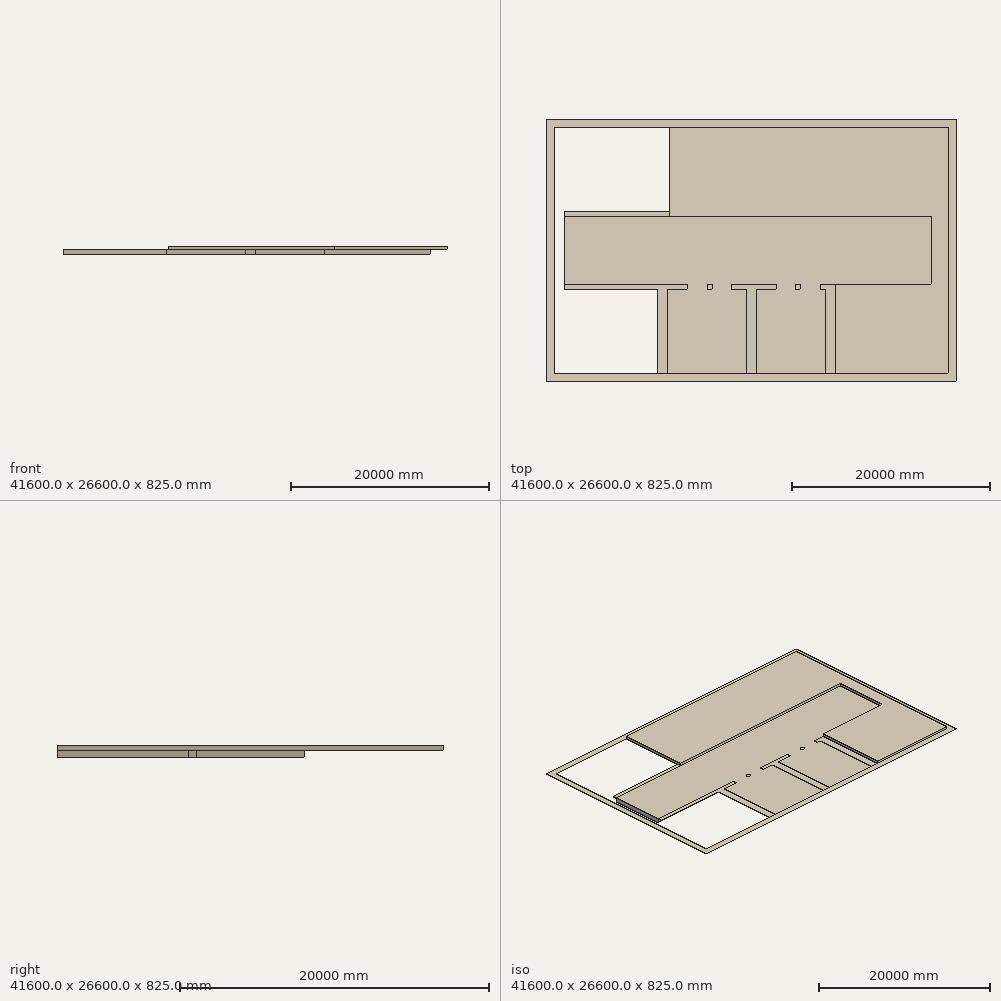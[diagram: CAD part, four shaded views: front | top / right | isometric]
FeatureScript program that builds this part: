
annotation { "Feature Type Name" : "Feature", "Feature Type Description" : "" }
export const myFeature = defineFeature(function(context is Context, id is Id, definition is map)
    precondition{}
    {
        {
            assignVariable(context, id + "F0", {"name" : "m", "anyValue" : 1});
        }
        {
            var Q0;
            Q0=qCreatedBy(makeId("Top.planeOp"),FACE);
            var sketch = newSketch(context, id + "F1", { "sketchPlane" : qUnion([Q0])});
            skLineSegment(sketch, "E0.bottom", {"start": v(-20000, -12500) * mm, "end": v(20000, -12500) * mm, "construction": true});
            skLineSegment(sketch, "E0.top", {"start": v(-20000, 12500) * mm, "end": v(20000, 12500) * mm, "construction": true});
            skLineSegment(sketch, "E0.left", {"start": v(-20000, -12500) * mm, "end": v(-20000, 12500) * mm, "construction": true});
            skLineSegment(sketch, "E0.right", {"start": v(20000, -12500) * mm, "end": v(20000, 12500) * mm, "construction": true});
            skPoint(sketch, "E0.middle", {"position": v(0, 0) * mm});
            skLineSegment(sketch, "E1", {"start": v(-19000, 3500) * mm, "end": v(6200, 3500) * mm});
            skLineSegment(sketch, "E2", {"start": v(-19000, -3500) * mm, "end": v(-9000, -3500) * mm});
            skPoint(sketch, "E2.endSnap0", {"position": v(20000, 0) * mm});
            skLineSegment(sketch, "E3", {"start": v(18800, 3500) * mm, "end": v(18800, -3500) * mm});
            skLineSegment(sketch, "E4", {"start": v(8000, 3500) * mm, "end": v(8000, 12500) * mm});
            skLineSegment(sketch, "E5", {"start": v(6200, 3500) * mm, "end": v(6200, 8500) * mm});
            skLineSegment(sketch, "E6", {"start": v(0, 4000) * mm, "end": v(0, 12500) * mm});
            skLineSegment(sketch, "E7", {"start": v(8000, -3500) * mm, "end": v(8000, -12500) * mm});
            skLineSegment(sketch, "E8", {"start": v(-9000, -3500) * mm, "end": v(-9000, -12500) * mm});
            skLineSegment(sketch, "E9.trimOffspring", {"start": v(8000, 3500) * mm, "end": v(18800, 3500) * mm});
            skLineSegment(sketch, "E10", {"start": v(3000, 8500) * mm, "end": v(3000, 12500) * mm});
            skPoint(sketch, "E11.start.orphan", {"position": v(6200, 12500) * mm});
            skLineSegment(sketch, "E12", {"start": v(0, -3500) * mm, "end": v(0, -12500) * mm});
            skLineSegment(sketch, "E13", {"start": v(3000, 8500) * mm, "end": v(8000, 8500) * mm});
            skLineSegment(sketch, "E14", {"start": v(-19000, 4000) * mm, "end": v(-500, 4000) * mm});
            skLineSegment(sketch, "E15", {"start": v(-500, 4000) * mm, "end": v(-500, 12500) * mm});
            skLineSegment(sketch, "E16", {"start": v(2500, 12500) * mm, "end": v(2500, 8000) * mm});
            skLineSegment(sketch, "E17", {"start": v(2500, 8000) * mm, "end": v(5700, 8000) * mm});
            skLineSegment(sketch, "E18", {"start": v(0, 4000) * mm, "end": v(5700, 4000) * mm});
            skLineSegment(sketch, "E19", {"start": v(8500, 12500) * mm, "end": v(8500, 4000) * mm});
            skLineSegment(sketch, "E20", {"start": v(8500, 4000) * mm, "end": v(18800, 4000) * mm});
            skLineSegment(sketch, "E21", {"start": v(5700, 8000) * mm, "end": v(5700, 4000) * mm});
            skPoint(sketch, "E21.endSnap0", {"position": v(3100, 4000) * mm});
            skLineSegment(sketch, "E22", {"start": v(18300, 3500) * mm, "end": v(18300, -3500) * mm});
            skLineSegment(sketch, "E23", {"start": v(8500, -12500) * mm, "end": v(8500, -4000) * mm});
            skLineSegment(sketch, "E24", {"start": v(8500, -4000) * mm, "end": v(9000, -4000) * mm});
            skLineSegment(sketch, "E25", {"start": v(-8500, -12500) * mm, "end": v(-8500, -4000) * mm});
            skLineSegment(sketch, "E26", {"start": v(-8500, -4000) * mm, "end": v(-6500, -4000) * mm});
            skLineSegment(sketch, "E27", {"start": v(-500, -4000) * mm, "end": v(-500, -12500) * mm});
            skLineSegment(sketch, "E28", {"start": v(-19000, -4000) * mm, "end": v(-9500, -4000) * mm});
            skLineSegment(sketch, "E29", {"start": v(-9500, -4000) * mm, "end": v(-9500, -12500) * mm});
            skLineSegment(sketch, "E30", {"start": v(500, -12500) * mm, "end": v(500, -4000) * mm});
            skLineSegment(sketch, "E31", {"start": v(500, -4000) * mm, "end": v(2500, -4000) * mm});
            skLineSegment(sketch, "E32", {"start": v(7500, -4000) * mm, "end": v(7500, -12500) * mm});
            skLineSegment(sketch, "E33", {"start": v(18800, 3500) * mm, "end": v(18800, 4000) * mm});
            skPoint(sketch, "E34.orphan", {"position": v(20000, -3500) * mm});
            skLineSegment(sketch, "E35", {"start": v(18800, -3500) * mm, "end": v(18800, -4000) * mm});
            skPoint(sketch, "E36.orphan", {"position": v(6200, 4000) * mm});
            skLineSegment(sketch, "E37", {"start": v(-500, -12500) * mm, "end": v(500, -12500) * mm});
            skLineSegment(sketch, "E38", {"start": v(-9500, -12500) * mm, "end": v(-8500, -12500) * mm});
            skLineSegment(sketch, "E39", {"start": v(-20000, -12500) * mm, "end": v(-19500, -12500) * mm});
            skLineSegment(sketch, "E40", {"start": v(-500, 12500) * mm, "end": v(0, 12500) * mm});
            skLineSegment(sketch, "E41", {"start": v(-20000, 3500) * mm, "end": v(-20000, 4000) * mm});
            skLineSegment(sketch, "E42", {"start": v(2500, 12500) * mm, "end": v(3000, 12500) * mm});
            skLineSegment(sketch, "E43", {"start": v(8000, 12500) * mm, "end": v(8500, 12500) * mm});
            skLineSegment(sketch, "E44", {"start": v(7500, -12500) * mm, "end": v(8500, -12500) * mm});
            skLineSegment(sketch, "E45", {"start": v(-20000, -3500) * mm, "end": v(-20000, -12500) * mm});
            skLineSegment(sketch, "E46", {"start": v(-19000, 3500) * mm, "end": v(-19000, -3500) * mm});
            skLineSegment(sketch, "E47", {"start": v(-19000, -3500) * mm, "end": v(-19000, -4000) * mm});
            skLineSegment(sketch, "E48", {"start": v(-19000, 3500) * mm, "end": v(-19000, 4000) * mm});
            skLineSegment(sketch, "E49", {"start": v(9000, -4000) * mm, "end": v(9000, -3500) * mm});
            skLineSegment(sketch, "E50", {"start": v(11000, -4000) * mm, "end": v(11000, -3500) * mm});
            skLineSegment(sketch, "E51.trimOffspring", {"start": v(11000, -4000) * mm, "end": v(18800, -4000) * mm});
            skLineSegment(sketch, "E52.trimOffspring", {"start": v(11000, -3500) * mm, "end": v(18300, -3500) * mm});
            skLineSegment(sketch, "E53", {"start": v(9000, 4000) * mm, "end": v(9000, 3500) * mm});
            skLineSegment(sketch, "E54", {"start": v(11000, 4000) * mm, "end": v(11000, 3500) * mm});
            skLineSegment(sketch, "E55", {"start": v(5700, 8000) * mm, "end": v(6200, 8000) * mm});
            skLineSegment(sketch, "E56", {"start": v(5700, 7000) * mm, "end": v(6200, 7000) * mm});
            skLineSegment(sketch, "E57", {"start": v(-9000, 4000) * mm, "end": v(-9000, 12500) * mm});
            skLineSegment(sketch, "E58", {"start": v(-11000, 4000) * mm, "end": v(-11000, 3500) * mm});
            skLineSegment(sketch, "E59", {"start": v(-9000, 4000) * mm, "end": v(-9000, 3500) * mm});
            skLineSegment(sketch, "E60", {"start": v(-6500, -4000) * mm, "end": v(-6500, -3500) * mm});
            skPoint(sketch, "E60.endSnap0", {"position": v(-5000, -3500) * mm});
            skLineSegment(sketch, "E61", {"start": v(-4500, -3500) * mm, "end": v(-4500, -4000) * mm});
            skLineSegment(sketch, "E62", {"start": v(-4000, -3500) * mm, "end": v(-4000, -4000) * mm});
            skLineSegment(sketch, "E63", {"start": v(-2000, -3500) * mm, "end": v(-2000, -4000) * mm});
            skLineSegment(sketch, "E64.trimOffspring", {"start": v(-4500, -4000) * mm, "end": v(-4000, -4000) * mm});
            skLineSegment(sketch, "E65.trimOffspring", {"start": v(-5000, -3500) * mm, "end": v(-4000, -3500) * mm});
            skLineSegment(sketch, "E66.trimOffspring", {"start": v(-2000, -3500) * mm, "end": v(2500, -3500) * mm});
            skLineSegment(sketch, "E67.trimOffspring", {"start": v(-2000, -4000) * mm, "end": v(-500, -4000) * mm});
            skLineSegment(sketch, "E68", {"start": v(2500, -3500) * mm, "end": v(2500, -4000) * mm});
            skLineSegment(sketch, "E69", {"start": v(4500, -3500) * mm, "end": v(4500, -4000) * mm});
            skLineSegment(sketch, "E70", {"start": v(5000, -3500) * mm, "end": v(5000, -4000) * mm});
            skLineSegment(sketch, "E71", {"start": v(7000, -3500) * mm, "end": v(7000, -4000) * mm});
            skLineSegment(sketch, "E72.trimOffspring", {"start": v(4500, -4000) * mm, "end": v(5000, -4000) * mm});
            skLineSegment(sketch, "E73.trimOffspring", {"start": v(4500, -3500) * mm, "end": v(5000, -3500) * mm});
            skLineSegment(sketch, "E74.trimOffspring", {"start": v(7000, -3500) * mm, "end": v(9000, -3500) * mm});
            skLineSegment(sketch, "E75.trimOffspring", {"start": v(7000, -4000) * mm, "end": v(7500, -4000) * mm});
            skLineSegment(sketch, "E76", {"start": v(-6500, -3500) * mm, "end": v(-9000, -3500) * mm});
            skSolve(sketch);
        }
        {
            var Q0;
            Q0 = qSketchRegion(id + "F1", true);
            extrude(context, id + "F2", {"entities" : qUnion([Q0]), "depth" : (getVariable(context, 'm') * 5) * mm});
        }
        {
            var Q0;
            Q0=qCreatedBy(makeId("Top.planeOp"),FACE);
            var sketch = newSketch(context, id + "F3", { "sketchPlane" : qUnion([Q0])});
            skLineSegment(sketch, "E77.bottom", {"start": v(-20000, 12500) * mm, "end": v(20000, 12500) * mm});
            skLineSegment(sketch, "E77.top", {"start": v(-20000, -12500) * mm, "end": v(20000, -12500) * mm});
            skLineSegment(sketch, "E77.left", {"start": v(-20000, 12500) * mm, "end": v(-20000, -12500) * mm});
            skLineSegment(sketch, "E77.right", {"start": v(20000, 12500) * mm, "end": v(20000, -12500) * mm});
            skPoint(sketch, "E77.middle", {"position": v(0, 0) * mm});
            skLineSegment(sketch, "E78.bottom", {"start": v(-20800, 13300) * mm, "end": v(20800, 13300) * mm});
            skLineSegment(sketch, "E78.top", {"start": v(-20800, -13300) * mm, "end": v(20800, -13300) * mm});
            skLineSegment(sketch, "E78.left", {"start": v(-20800, 13300) * mm, "end": v(-20800, -13300) * mm});
            skLineSegment(sketch, "E78.right", {"start": v(20800, 13300) * mm, "end": v(20800, -13300) * mm});
            skSolve(sketch);
        }
        {
            var Q0;
            Q0 = qSketchRegion(id + "F3", true);
            extrude(context, id + "F4", {"entities" : qUnion([Q0]), "depth" : (getVariable(context, 'm') * 5) * mm, "offsetDistance" : 25 * mm});
        }
        {
            var Q0;
            Q0=makeQuery(id+"F4.boolean.opBoolean","MERGE",FACE,{"derivedFrom":[makeQuery(id+"F2.opExtrude","CAP_FACE",FACE,{"disambiguationData":[OSD([sQuery(id+"F1.wireOp",EDGE,"E1"),sQuery(id+"F1.wireOp",EDGE,"E5"),sQuery(id+"F1.wireOp",EDGE,"E6"),sQuery(id+"F1.wireOp",EDGE,"E10"),sQuery(id+"F1.wireOp",EDGE,"E13"),sQuery(id+"F1.wireOp",EDGE,"E14"),sQuery(id+"F1.wireOp",EDGE,"E15"),sQuery(id+"F1.wireOp",EDGE,"E16"),sQuery(id+"F1.wireOp",EDGE,"E17"),sQuery(id+"F1.wireOp",EDGE,"E18"),sQuery(id+"F1.wireOp",EDGE,"E21"),sQuery(id+"F1.wireOp",EDGE,"E40"),sQuery(id+"F1.wireOp",EDGE,"E41"),sQuery(id+"F1.wireOp",EDGE,"E42")])],"isStart":true}),makeQuery(id+"F2.opExtrude","CAP_FACE",FACE,{"disambiguationData":[OSD([sQuery(id+"F1.wireOp",EDGE,"E2"),sQuery(id+"F1.wireOp",EDGE,"E3"),sQuery(id+"F1.wireOp",EDGE,"E4"),sQuery(id+"F1.wireOp",EDGE,"E9.trimOffspring"),sQuery(id+"F1.wireOp",EDGE,"E19"),sQuery(id+"F1.wireOp",EDGE,"E20"),sQuery(id+"F1.wireOp",EDGE,"E22"),sQuery(id+"F1.wireOp",EDGE,"E23"),sQuery(id+"F1.wireOp",EDGE,"E24"),sQuery(id+"F1.wireOp",EDGE,"E25"),sQuery(id+"F1.wireOp",EDGE,"E26"),sQuery(id+"F1.wireOp",EDGE,"E27"),sQuery(id+"F1.wireOp",EDGE,"Nue6VRTW-FETu-XBWY-EpAh-Sq0DysgrU8W1"),sQuery(id+"F1.wireOp",EDGE,"E28"),sQuery(id+"F1.wireOp",EDGE,"E29"),sQuery(id+"F1.wireOp",EDGE,"E30"),sQuery(id+"F1.wireOp",EDGE,"E31"),sQuery(id+"F1.wireOp",EDGE,"E32"),sQuery(id+"F1.wireOp",EDGE,"E33"),sQuery(id+"F1.wireOp",EDGE,"E35"),sQuery(id+"F1.wireOp",EDGE,"E37"),sQuery(id+"F1.wireOp",EDGE,"E38"),sQuery(id+"F1.wireOp",EDGE,"E43"),sQuery(id+"F1.wireOp",EDGE,"E44"),sQuery(id+"F1.wireOp",EDGE,"E39"),sQuery(id+"F1.wireOp",EDGE,"E45")])],"isStart":true}),makeQuery(id+"F4.opExtrude","CAP_FACE",FACE,{"disambiguationData":[OSD([sQuery(id+"F3.wireOp",EDGE,"E77.bottom"),sQuery(id+"F3.wireOp",EDGE,"E77.top"),sQuery(id+"F3.wireOp",EDGE,"E77.left"),sQuery(id+"F3.wireOp",EDGE,"E77.right"),sQuery(id+"F3.wireOp",EDGE,"E78.bottom"),sQuery(id+"F3.wireOp",EDGE,"E78.top"),sQuery(id+"F3.wireOp",EDGE,"E78.left"),sQuery(id+"F3.wireOp",EDGE,"E78.right")])],"isStart":true})]});
            var sketch = newSketch(context, id + "F5", { "sketchPlane" : qUnion([Q0])});
            skLineSegment(sketch, "E79.bottom", {"start": v(-19000, -3500) * mm, "end": v(18300, -3500) * mm});
            skLineSegment(sketch, "E79.top", {"start": v(-19000, 3500) * mm, "end": v(-6500, 3500) * mm});
            skLineSegment(sketch, "E79.left", {"start": v(-19000, -3500) * mm, "end": v(-19000, 3500) * mm});
            skLineSegment(sketch, "E79.right", {"start": v(18300, -3500) * mm, "end": v(18300, 3500) * mm});
            skLineSegment(sketch, "E80.bottom", {"start": v(-8500, 4000) * mm, "end": v(-6500, 4000) * mm});
            skLineSegment(sketch, "E80.top", {"start": v(-8500, 12500) * mm, "end": v(-500, 12500) * mm});
            skLineSegment(sketch, "E80.left", {"start": v(-8500, 4000) * mm, "end": v(-8500, 12500) * mm});
            skLineSegment(sketch, "E80.right", {"start": v(-500, 4000) * mm, "end": v(-500, 12500) * mm});
            skLineSegment(sketch, "E81.bottom", {"start": v(500, 4000) * mm, "end": v(2500, 4000) * mm});
            skLineSegment(sketch, "E81.top", {"start": v(500, 12500) * mm, "end": v(7500, 12500) * mm});
            skLineSegment(sketch, "E81.left", {"start": v(500, 4000) * mm, "end": v(500, 12500) * mm});
            skLineSegment(sketch, "E81.right", {"start": v(7500, 4000) * mm, "end": v(7500, 12500) * mm});
            skLineSegment(sketch, "E82", {"start": v(-6500, 4000) * mm, "end": v(-6500, 3500) * mm});
            skLineSegment(sketch, "E83", {"start": v(-4500, 3500) * mm, "end": v(-4500, 4000) * mm});
            skLineSegment(sketch, "E84", {"start": v(-4000, 3500) * mm, "end": v(-4000, 4000) * mm});
            skLineSegment(sketch, "E85", {"start": v(-500, 4000) * mm, "end": v(500, 4000) * mm, "construction": true});
            skLineSegment(sketch, "E86", {"start": v(0, 4000) * mm, "end": v(0, 3500) * mm, "construction": true});
            skLineSegment(sketch, "E87", {"start": v(-2000, 3500) * mm, "end": v(-2000, 4000) * mm});
            skLineSegment(sketch, "E88.MirrorCS", {"start": v(4500, 3500) * mm, "end": v(4500, 4000) * mm});
            skLineSegment(sketch, "E89", {"start": v(2500, 3500) * mm, "end": v(2500, 4000) * mm});
            skLineSegment(sketch, "E90", {"start": v(5000, 3500) * mm, "end": v(5000, 4000) * mm});
            skLineSegment(sketch, "E91", {"start": v(7000, 3500) * mm, "end": v(7000, 4000) * mm});
            skLineSegment(sketch, "E92.trimOffspring", {"start": v(-4500, 4000) * mm, "end": v(-4000, 4000) * mm});
            skLineSegment(sketch, "E93.trimOffspring", {"start": v(-4500, 3500) * mm, "end": v(-4000, 3500) * mm});
            skLineSegment(sketch, "E94.trimOffspring", {"start": v(-2000, 4000) * mm, "end": v(-500, 4000) * mm});
            skLineSegment(sketch, "E95.trimOffspring", {"start": v(-2000, 3500) * mm, "end": v(2500, 3500) * mm});
            skLineSegment(sketch, "E96.trimOffspring", {"start": v(4500, 4000) * mm, "end": v(5000, 4000) * mm});
            skLineSegment(sketch, "E97.trimOffspring", {"start": v(7000, 4000) * mm, "end": v(7500, 4000) * mm});
            skLineSegment(sketch, "E98.trimOffspring", {"start": v(7000, 3500) * mm, "end": v(18300, 3500) * mm});
            skLineSegment(sketch, "E99.trimOffspring", {"start": v(4500, 3500) * mm, "end": v(5000, 3500) * mm});
            skSolve(sketch);
        }
        {
            var Q0;
            Q0 = qSketchRegion(id + "F5", true);
            extrude(context, id + "F6", {"entities" : qUnion([Q0]), "depth" : getVariable(context, 'm') * 500 * mm, "offsetDistance" : 25 * mm});
        }
        {
            var Q0;
            Q0=makeQuery(id+"F4.opExtrude","CAP_FACE",FACE,{"disambiguationData":[OSD([sQuery(id+"F3.wireOp",EDGE,"E77.bottom"),sQuery(id+"F3.wireOp",EDGE,"E77.top"),sQuery(id+"F3.wireOp",EDGE,"E77.left"),sQuery(id+"F3.wireOp",EDGE,"E77.right"),sQuery(id+"F3.wireOp",EDGE,"E78.bottom"),sQuery(id+"F3.wireOp",EDGE,"E78.top"),sQuery(id+"F3.wireOp",EDGE,"E78.left"),sQuery(id+"F3.wireOp",EDGE,"E78.right")])],"isStart":true});
            var sketch = newSketch(context, id + "F7", { "sketchPlane" : qUnion([Q0])});
            skLineSegment(sketch, "E100", {"start": v(8500, 12500) * mm, "end": v(8500, 3500) * mm});
            skLineSegment(sketch, "E101", {"start": v(8500, 3500) * mm, "end": v(18300, 3500) * mm});
            skLineSegment(sketch, "E102", {"start": v(18300, 3500) * mm, "end": v(18300, -3500) * mm});
            skLineSegment(sketch, "E103", {"start": v(18300, -3500) * mm, "end": v(8704.21, -3500) * mm});
            skLineSegment(sketch, "E104", {"start": v(8704.21, -3500) * mm, "end": v(-8273.78, -3500) * mm});
            skLineSegment(sketch, "E105", {"start": v(-8273.78, -3500) * mm, "end": v(-8273.78, -12500) * mm});
            skLineSegment(sketch, "E106", {"start": v(-8273.78, -12500) * mm, "end": v(20000, -12500) * mm});
            skLineSegment(sketch, "E107", {"start": v(20000, -12500) * mm, "end": v(20000, 12500) * mm});
            skLineSegment(sketch, "E108", {"start": v(8500, 12500) * mm, "end": v(20000, 12500) * mm});
            skSolve(sketch);
        }
        {
            var Q0;
            Q0 = qSketchRegion(id + "F7", true);
            extrude(context, id + "F8", {"entities" : qUnion([Q0]), "oppositeDirection" : true, "depth" : 325 * mm, "offsetDistance" : 25 * mm});
        }
    });
